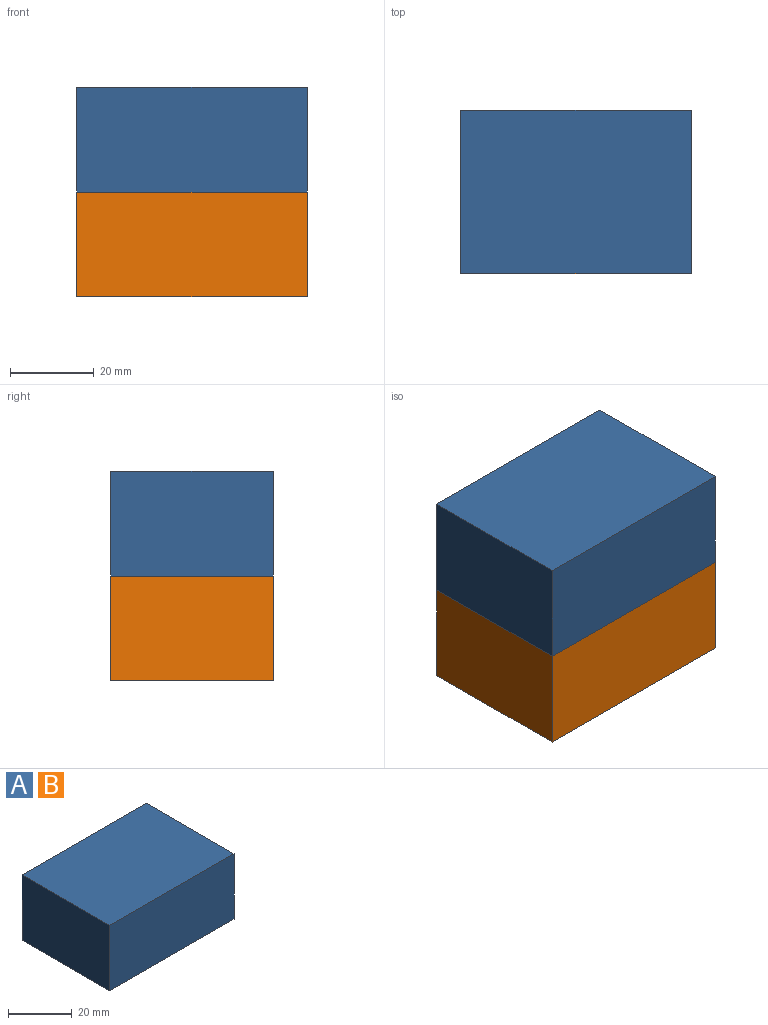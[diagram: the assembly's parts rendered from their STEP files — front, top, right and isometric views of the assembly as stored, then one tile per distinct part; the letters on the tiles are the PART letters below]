
ASSEMBLY  parts=2 mates=1
PART A: 6 faces, bbox 54.9x38.8x25 mm
  f0: plane 54.92x25mm, normal (0,1,0), area 1373.1mm2, adj f1,f3,f4,f5
  f1: plane 38.79x25mm, normal (-1,0,0), area 969.8mm2, adj f0,f2,f4,f5
  f2: plane 54.92x25mm, normal (0,-1,0), area 1373.1mm2, adj f1,f3,f4,f5
  f3: plane 38.79x25mm, normal (1,0,0), area 969.8mm2, adj f0,f2,f4,f5
  f4: plane 54.92x38.79mm, normal (0,0,1), area 2130.5mm2, adj f0,f1,f2,f3
  f5: plane 54.92x38.79mm, normal (0,0,-1), area 2130.5mm2, adj f0,f1,f2,f3
PART B: same geometry as A
PLACE A t=(-2.2,56.41,21.14)mm
PLACE B t=(-2.2,56.41,-3.86)mm
MATE parallel B.f4 <-> A.f5  axis (0,0,1) through (25.26,37.01,21.14)mm
